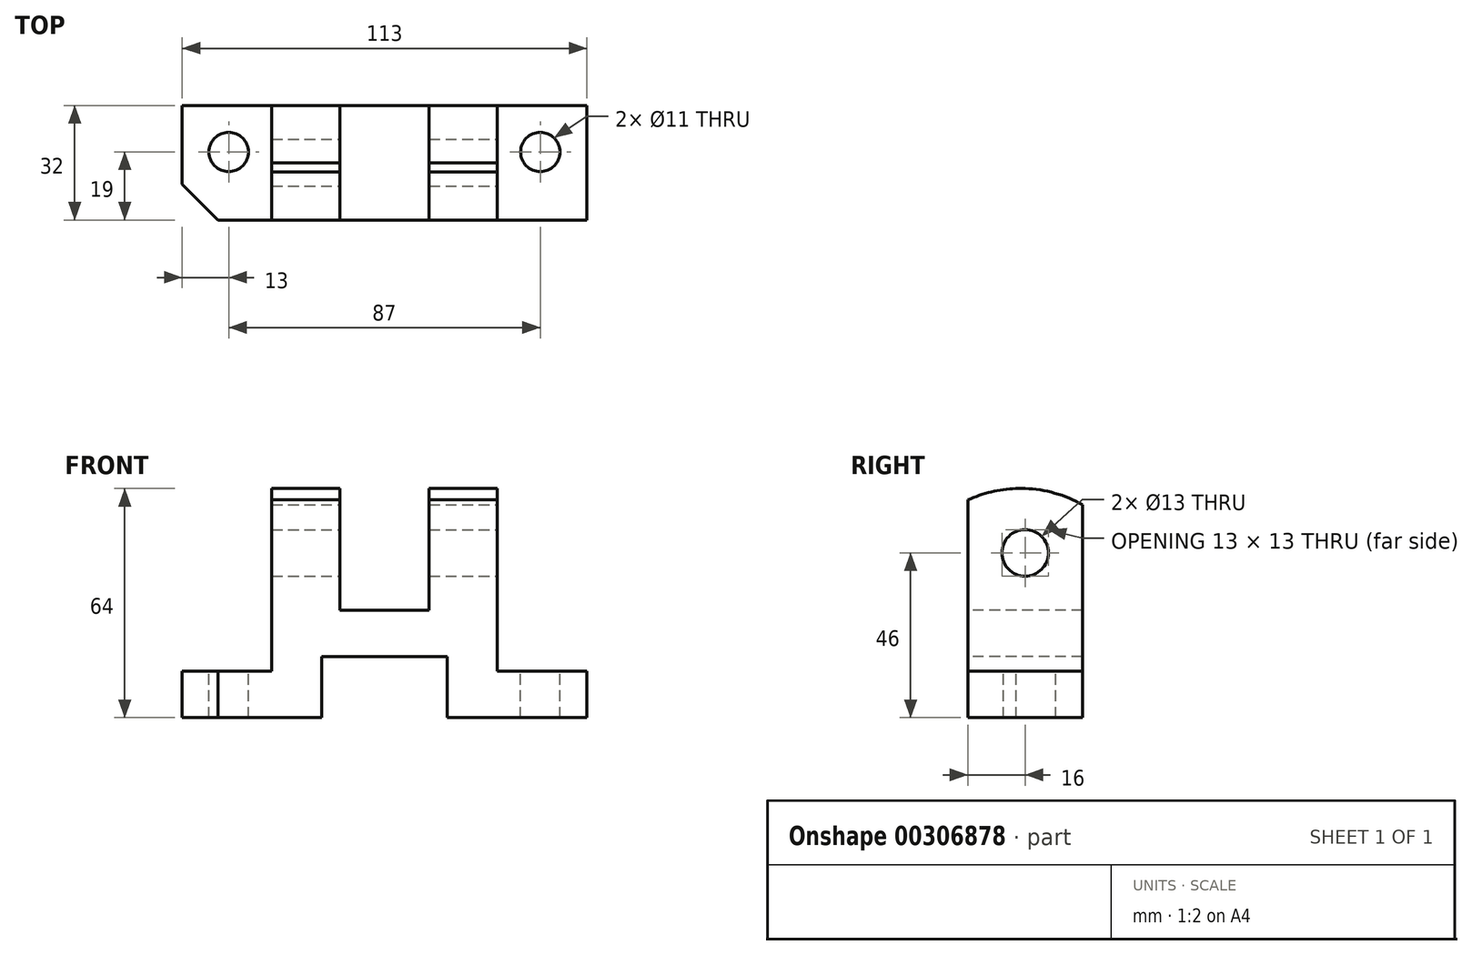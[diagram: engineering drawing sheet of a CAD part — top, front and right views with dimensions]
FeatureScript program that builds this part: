
annotation { "Feature Type Name" : "Feature", "Feature Type Description" : "" }
export const myFeature = defineFeature(function(context is Context, id is Id, definition is map)
    precondition{}
    {
        {
            var Q0;
            Q0=qCreatedBy(makeId("Front.planeOp"),FACE);
            var sketch = newSketch(context, id + "F0", { "sketchPlane" : qUnion([Q0])});
            skLineSegment(sketch, "E0", {"start": v(0, 0) * mm, "end": v(39, 0) * mm});
            skLineSegment(sketch, "E1", {"start": v(39, 0) * mm, "end": v(39, 17) * mm});
            skLineSegment(sketch, "E2", {"start": v(39, 17) * mm, "end": v(74, 17) * mm});
            skLineSegment(sketch, "E3", {"start": v(74, 17) * mm, "end": v(74, 0) * mm});
            skLineSegment(sketch, "E4", {"start": v(74, 0) * mm, "end": v(113, 0) * mm});
            skLineSegment(sketch, "E5", {"start": v(113, 0) * mm, "end": v(113, 13) * mm});
            skLineSegment(sketch, "E6", {"start": v(113, 13) * mm, "end": v(88, 13) * mm});
            skLineSegment(sketch, "E7", {"start": v(88, 13) * mm, "end": v(88, 64) * mm});
            skLineSegment(sketch, "E8", {"start": v(88, 64) * mm, "end": v(69, 64) * mm});
            skLineSegment(sketch, "E9", {"start": v(69, 64) * mm, "end": v(69, 30) * mm});
            skLineSegment(sketch, "E10", {"start": v(69, 30) * mm, "end": v(44, 30) * mm});
            skLineSegment(sketch, "E11", {"start": v(44, 30) * mm, "end": v(44, 64) * mm});
            skLineSegment(sketch, "E12", {"start": v(44, 64) * mm, "end": v(25, 64) * mm});
            skLineSegment(sketch, "E13", {"start": v(25, 64) * mm, "end": v(25, 13) * mm});
            skLineSegment(sketch, "E14", {"start": v(25, 13) * mm, "end": v(0, 13) * mm});
            skLineSegment(sketch, "E15", {"start": v(0, 13) * mm, "end": v(0, 0) * mm});
            skSolve(sketch);
        }
        {
            var Q0;
            Q0=makeQuery(id+"F0.imprint","IMPRINT",FACE,{"disambiguationData":[TD([[makeQuery(id+"F0.imprint","IMPRINT",EDGE,{"derivedFrom":sQuery(id+"F0.wireOp",EDGE,"E0")}),1.0]])]});
            extrude(context, id + "F1", {"entities" : qUnion([Q0]), "oppositeDirection" : true, "depth" : 32 * mm});
        }
        {
            var Q0;
            Q0=makeQuery(id+"F1.opExtrude","SWEPT_FACE",FACE,{"disambiguationData":[OSD([sQuery(id+"F0.wireOp",EDGE,"E7")])]});
            var sketch = newSketch(context, id + "F2", { "sketchPlane" : qUnion([Q0])});
            skLineSegment(sketch, "E16", {"start": v(16, -103.9) * mm, "end": v(16, 103.9) * mm, "construction": true});
            skCircle(sketch, "E17", {"center": v(16, 46) * mm, "radius": 6.5 * mm});
            skLineSegment(sketch, "E18.0.0", {"start": v(0, 64) * mm, "end": v(0, 13) * mm});
            skLineSegment(sketch, "E18.0.1", {"start": v(0, 13) * mm, "end": v(32, 13) * mm});
            skLineSegment(sketch, "E18.0.2", {"start": v(32, 13) * mm, "end": v(32, 64) * mm});
            skLineSegment(sketch, "E18.0.3", {"start": v(32, 64) * mm, "end": v(0, 64) * mm});
            skLineSegment(sketch, "E19.0.0", {"start": v(0, 13) * mm, "end": v(0, 0) * mm});
            skLineSegment(sketch, "E19.0.1", {"start": v(0, 0) * mm, "end": v(32, 0) * mm});
            skLineSegment(sketch, "E19.0.2", {"start": v(32, 0) * mm, "end": v(32, 13) * mm});
            skLineSegment(sketch, "E19.0.3", {"start": v(32, 13) * mm, "end": v(0, 13) * mm});
            skSolve(sketch);
        }
        {
            var Q0;
            Q0=makeQuery(id+"F2.imprint","IMPRINT",FACE,{"disambiguationData":[TD([[makeQuery(id+"F2.imprint","IMPRINT",EDGE,{"derivedFrom":sQuery(id+"F2.wireOp",EDGE,"E17")}),1.0]])]});
            extrude(context, id + "F3", {"entities" : qUnion([Q0]), "operationType" : NewBodyOperationType.REMOVE, "endBound" : BoundingType.THROUGH_ALL, "oppositeDirection" : true, "depth" : 25 * mm});
        }
        {
            var Q0;
            Q0=makeQuery(id+"F1.opExtrude","SWEPT_FACE",FACE,{"disambiguationData":[OSD([sQuery(id+"F0.wireOp",EDGE,"E7")])]});
            var sketch = newSketch(context, id + "F4", { "sketchPlane" : qUnion([Q0])});
            skArc(sketch, "E20", {"start": v(32, 59.45) * mm, "mid": v(16.16, 64) * mm, "end": v(0, 60.8) * mm});
            skLineSegment(sketch, "E21.0.0", {"start": v(0, 64) * mm, "end": v(0, 13) * mm});
            skLineSegment(sketch, "E21.0.1", {"start": v(0, 13) * mm, "end": v(32, 13) * mm});
            skLineSegment(sketch, "E21.0.2", {"start": v(32, 13) * mm, "end": v(32, 64) * mm});
            skLineSegment(sketch, "E21.0.3", {"start": v(32, 64) * mm, "end": v(0, 64) * mm});
            skLineSegment(sketch, "E22.0.0", {"start": v(0, 13) * mm, "end": v(0, 0) * mm});
            skLineSegment(sketch, "E22.0.1", {"start": v(0, 0) * mm, "end": v(32, 0) * mm});
            skLineSegment(sketch, "E22.0.2", {"start": v(32, 0) * mm, "end": v(32, 13) * mm});
            skLineSegment(sketch, "E22.0.3", {"start": v(32, 13) * mm, "end": v(0, 13) * mm});
            skSolve(sketch);
        }
        {
            var Q0;
            {var subQ0=sQuery(id+"F4.wireOp",EDGE,"E20");var subQ1=sQuery(id+"F0.wireOp",EDGE,"E7");var subQ2=makeQuery(id+"F1.opExtrude","CAP_EDGE",EDGE,{"disambiguationData":[OSD([subQ1])],"isStart":true});var subQ3=makeQuery(id+"F4.imprint","INTERSECT",VERTEX,{"derivedFrom":[subQ2,subQ0]});Q0=makeQuery(id+"F4.imprint","IMPRINT",FACE,{"disambiguationData":[TD([[makeQuery(id+"F4.imprint","IMPRINT",EDGE,{"disambiguationData":[TD([[subQ3,1.0]])],"derivedFrom":subQ0}),-1.0]])]});}
            var Q1;
            {var subQ0=sQuery(id+"F4.wireOp",EDGE,"E20");var subQ1=sQuery(id+"F0.wireOp",EDGE,"E7");var subQ2=makeQuery(id+"F1.opExtrude","CAP_EDGE",EDGE,{"disambiguationData":[OSD([subQ1])],"isStart":false});var subQ3=makeQuery(id+"F4.imprint","INTERSECT",VERTEX,{"derivedFrom":[subQ2,subQ0]});Q1=makeQuery(id+"F4.imprint","IMPRINT",FACE,{"disambiguationData":[TD([[makeQuery(id+"F4.imprint","IMPRINT",EDGE,{"disambiguationData":[TD([[subQ3,-1.0]])],"derivedFrom":subQ0}),-1.0]])]});}
            extrude(context, id + "F5", {"entities" : qUnion([Q0, Q1]), "operationType" : NewBodyOperationType.REMOVE, "endBound" : BoundingType.THROUGH_ALL, "oppositeDirection" : true, "depth" : 25 * mm});
        }
        {
            var Q0;
            Q0=makeQuery(id+"F1.opExtrude","SWEPT_FACE",FACE,{"disambiguationData":[OSD([sQuery(id+"F0.wireOp",EDGE,"E14")])]});
            var sketch = newSketch(context, id + "F6", { "sketchPlane" : qUnion([Q0])});
            skLineSegment(sketch, "E23.0.0", {"start": v(88, 0) * mm, "end": v(113, 0) * mm});
            skLineSegment(sketch, "E23.0.1", {"start": v(113, 0) * mm, "end": v(113, 32) * mm});
            skLineSegment(sketch, "E23.0.2", {"start": v(113, 32) * mm, "end": v(88, 32) * mm});
            skLineSegment(sketch, "E23.0.3", {"start": v(88, 32) * mm, "end": v(88, 0) * mm});
            skCircle(sketch, "E24", {"center": v(13, 19) * mm, "radius": 5.5 * mm});
            skCircle(sketch, "E25", {"center": v(100, 19) * mm, "radius": 5.5 * mm});
            skLineSegment(sketch, "E26", {"start": v(0, 0) * mm, "end": v(10, 0) * mm});
            skLineSegment(sketch, "E27", {"start": v(10, 0) * mm, "end": v(0, 10) * mm});
            skLineSegment(sketch, "E28", {"start": v(0, 10) * mm, "end": v(0, 0) * mm});
            skLineSegment(sketch, "E29", {"start": v(113, 0) * mm, "end": v(113, 10) * mm});
            skLineSegment(sketch, "E30", {"start": v(113, 10) * mm, "end": v(103, 0) * mm});
            skLineSegment(sketch, "E31", {"start": v(103, 0) * mm, "end": v(113, 0) * mm});
            skSolve(sketch);
        }
        {
            var Q0;
            Q0=makeQuery(id+"F6.imprint","IMPRINT",FACE,{"disambiguationData":[TD([[makeQuery(id+"F6.imprint","IMPRINT",EDGE,{"derivedFrom":sQuery(id+"F6.wireOp",EDGE,"E26")}),-1.0]])]});
            var Q1;
            Q1=makeQuery(id+"F6.imprint","IMPRINT",FACE,{"disambiguationData":[TD([[makeQuery(id+"F6.imprint","IMPRINT",EDGE,{"derivedFrom":sQuery(id+"F6.wireOp",EDGE,"E29")}),1.0]])]});
            var Q2;
            Q2=makeQuery(id+"F6.imprint","IMPRINT",FACE,{"disambiguationData":[TD([[makeQuery(id+"F6.imprint","IMPRINT",EDGE,{"derivedFrom":sQuery(id+"F6.wireOp",EDGE,"E25")}),1.0]])]});
            extrude(context, id + "F7", {"entities" : qUnion([Q0, Q1, Q2]), "operationType" : NewBodyOperationType.REMOVE, "endBound" : BoundingType.THROUGH_ALL, "oppositeDirection" : true, "depth" : 25 * mm});
        }
        {
            var Q0;
            Q0=makeQuery(id+"F6.imprint","IMPRINT",FACE,{"disambiguationData":[TD([[makeQuery(id+"F6.imprint","IMPRINT",EDGE,{"derivedFrom":sQuery(id+"F6.wireOp",EDGE,"E24")}),1.0]])]});
            extrude(context, id + "F8", {"entities" : qUnion([Q0]), "operationType" : NewBodyOperationType.REMOVE, "endBound" : BoundingType.THROUGH_ALL, "oppositeDirection" : true, "depth" : 25 * mm});
        }
    });
